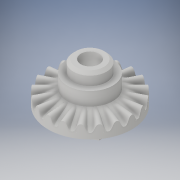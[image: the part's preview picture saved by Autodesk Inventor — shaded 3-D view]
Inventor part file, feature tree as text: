
AUTODESK INVENTOR PART (.ipt)
format: ipt  version: 2019.3 (Build 233278000, 278)  size: 636,416 bytes
history: native  units: in
note: dims shown in document units (in); Inventor stores cm internally (conversion verified against a paired STEP export)
features: sketch x6, other x4, hole x3, plane x2, extrude x1, revolve x1, sweep x1, split x1, pattern_circular x1
ambient origin geometry x8: Origin, YZ Plane, XZ Plane, XY Plane, X Axis, Y Axis, Z Axis, Center Point
bodies: Solid1 (feature_tree)
feature tree (20):
  extrude  "Extrusion1"  Depth=0.15in TaperAngle=0.0deg
  revolve  "Revolution1"  [1 undecoded]
  sweep  "Sweep1"
  sketch  "Sketch8"  dims[d10=135.0deg]
  split  "Split1"
  pattern_circular  "Circular Pattern1"  [2 undecoded]
  hole  "Hole1"  [1 undecoded]
  hole  "Hole2"  [1 undecoded]
  sketch  "Sketch9"  dims[d11=0.1in d12=0.154in d13=90.0deg d14=0.278in d15=0.75in d16=0.119in d17=0.25in d18=0.5635in d19=0.24in d20=0.0in d21=1.0in d22=1.0in d23=0.204in d24=0.75in d25=0.119in d26=0.25in d27=0.5635in d28=0.24in d29=0.0in d30=0.145in d35=0.0in d36=0.0in d37=7.874in d38=360.0deg d40=0.08in d43=45.0deg d44=45.0deg d57=1.0in d58=1.0in d47=0.163in d48=0.394in d49=0.417in d50=0.118in d51=90.0deg d52=0.559in d53=0.0in d54=0.2in d65=0.0444in d45=1.0in d46=1.0in d55=0.375in]
  plane  "Work Plane1"
  plane  "Work Plane2"
  other  "Work Point1"
  other  "Work Point2"
  hole  "Hole3"  [1 undecoded]
  sketch  "Sketch1"  dims[d0=0.476in d1=0.15in d2=0.0in]
  sketch  "Sketch3"  dims[d4=0.4635in d5=0.062in]
  sketch  "Sketch4"  dims[d6=0.166in d8=0.2515in]
  other  "tooth"
  sketch  "Sketch6"  dims[d9=0.15in]
  other  "Work Axis1"
note: 6 required parameter values undecoded (feature->parameter linkage not recoverable at this tier; creation-order binding heuristic only, values carry confidence <= 0.55)